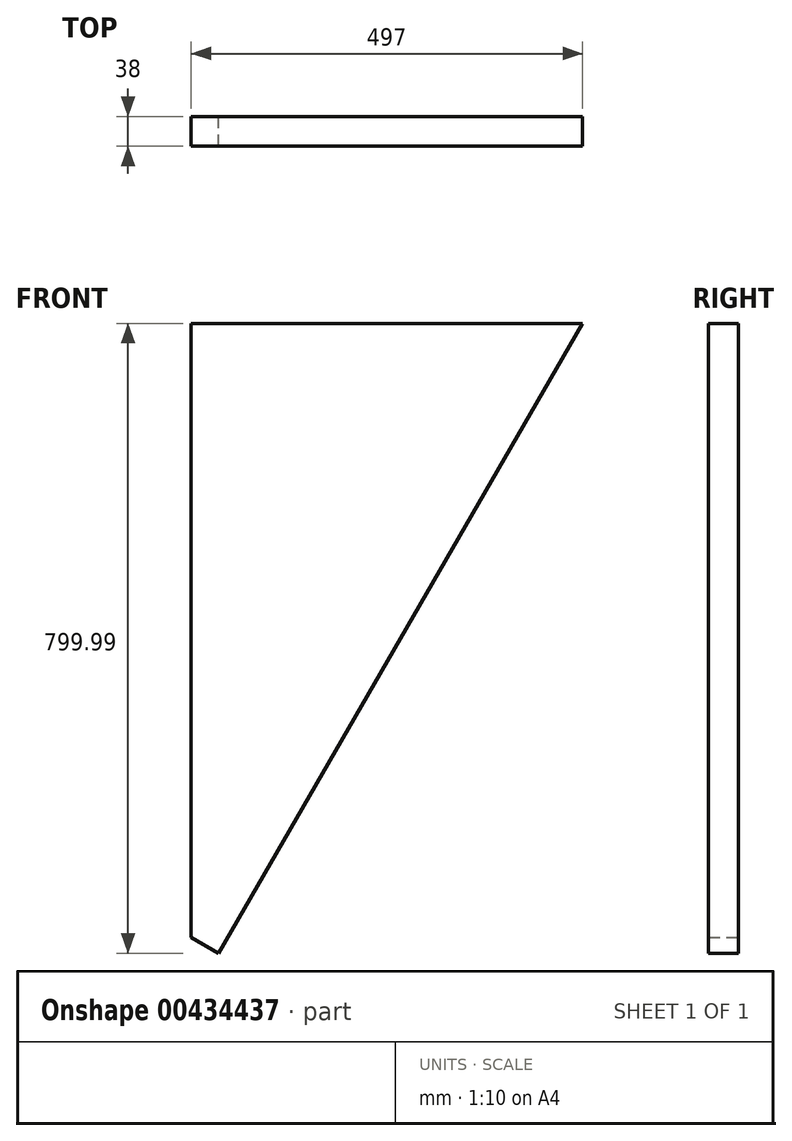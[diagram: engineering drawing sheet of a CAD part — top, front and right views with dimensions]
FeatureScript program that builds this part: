
annotation { "Feature Type Name" : "Feature", "Feature Type Description" : "" }
export const myFeature = defineFeature(function(context is Context, id is Id, definition is map)
    precondition{}
    {
        {
            var Q0;
            Q0=qCreatedBy(makeId("Front.planeOp"),FACE);
            var sketch = newSketch(context, id + "F0", { "sketchPlane" : qUnion([Q0])});
            skLineSegment(sketch, "E0.bottom", {"start": v(0, 0) * mm, "end": v(497, 0) * mm});
            skLineSegment(sketch, "E0.left", {"start": v(0, 0) * mm, "end": v(0, -779.98) * mm});
            skLineSegment(sketch, "E1", {"start": v(0, -779.98) * mm, "end": v(34.63, -800) * mm});
            skLineSegment(sketch, "E2", {"start": v(34.63, -800) * mm, "end": v(497, 0) * mm});
            skSolve(sketch);
        }
        {
            var Q0;
            Q0=qSketchRegion(id+"F0",true);
            extrude(context, id + "F1", {"entities" : qUnion([Q0]), "endBound" : BoundingType.SYMMETRIC, "depth" : 38 * mm, "offsetDistance" : 25 * mm});
        }
    });
